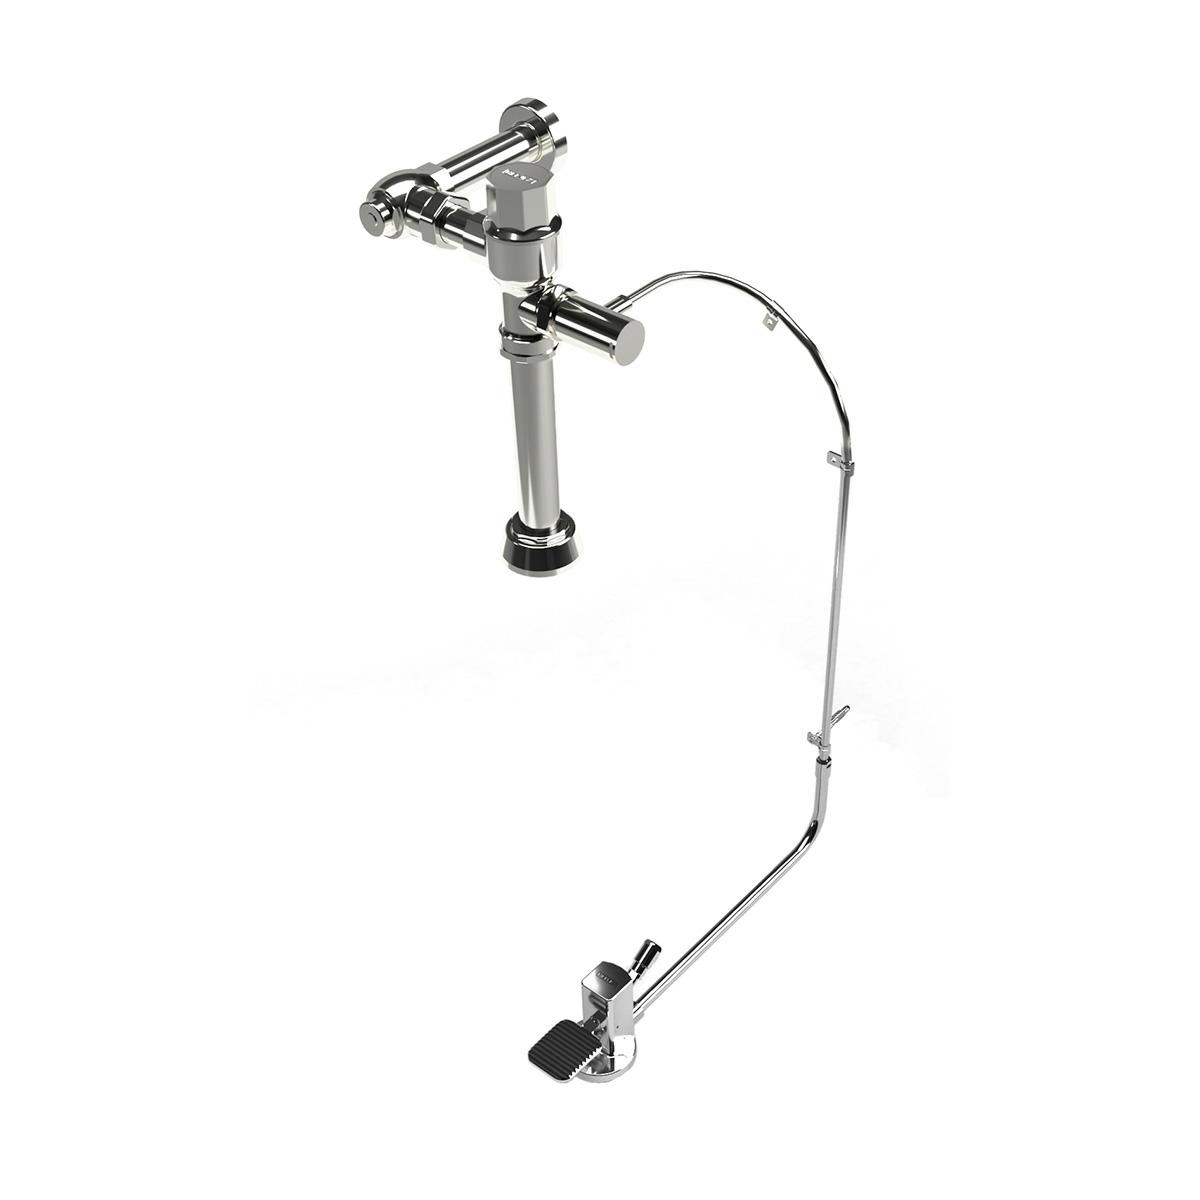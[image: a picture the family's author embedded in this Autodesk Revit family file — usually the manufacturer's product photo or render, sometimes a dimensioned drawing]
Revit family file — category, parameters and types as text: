
# Revit family: 313-38-4.8
name_source: partatom
category: Aparatos sanitarios
units: mm (PartAtom-declared; Revit-internal decimal feet)

## family parameters
Compartido = Sí
Corte con vacíos al cargar = No
Cota de conector redondo = Diámetro de uso
Número OmniClass = 23.45.00.00
Punto de cálculo de habitación = No
Se basa en plano de trabajo = No
Siempre vertical = Sí
Tipo de pieza = Normal
Título OmniClass = Sanitary, Laundry, and Cleaning Equipment

## types (1)
- 313-38-4.8
    Chrome = Brass Chromed
    Comentarios de tipo = Fluxómetro de pedal expuesto 4.8 LPD
    Conexión AF = Sí
    Connection = Conexión de alimentación: tubo 25,4 mm
    Descripción = Fluxómetro de pedal expuesto 4.8 LPD
    Documentation = https://www.helvex.com.mx
    Elevación por defecto = 0"
    Fabricante = HELVEX
    Imagen de tipo = 313-38-4.8.jpg
    Instructive = https://www.helvex.com.mx
    Max. Working Pressure = 85.3 psi
    Min. Working Pressure = 14.2 psi
    Modelo = 313-38-4.8
    Note = La tubería de alimentación debe tener un diámetro 32mm mínimo y debe conectarse una reducción de campana de 32mm - 25mm a la llave de
retención.
    URL = https://www.helvex.com.mx

## geometry (parser evidence)
native form markers: Sweep x3
no freeform markers — native parametric forms only
